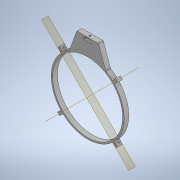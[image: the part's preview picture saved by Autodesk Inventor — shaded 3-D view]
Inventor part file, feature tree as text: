
AUTODESK INVENTOR PART (.ipt)
format: ipt  version: 2021.1 (Build 251245010, 245A)  size: 246,272 bytes
history: native  units: in
note: dims shown in document units (in); Inventor stores cm internally (conversion verified against a paired STEP export)
features: sketch x11, extrude x8, hole x2, plane x2, fillet x2, pattern_circular x1
ambient origin geometry x8: Origin, YZ Plane, XZ Plane, XY Plane, X Axis, Y Axis, Z Axis, Center Point
bodies: Solid1 (feature_tree)
feature tree (26):
  extrude  "Extrusion1"  Depth=0.75in TaperAngle=0.0deg
  extrude  "Extrusion2"  TaperAngle=0.0deg  [1 undecoded]
  extrude  "Extrusion3"  TaperAngle=45.0deg  [1 undecoded]
  extrude  "Extrusion4"  TaperAngle=45.0deg  [1 undecoded]
  sketch  "Sketch6"  dims[d47=0.25in d48=45.0deg]
  hole  "Hole2"  [1 undecoded]
  plane  "Work Plane1"
  plane  "Work Plane2"
  extrude  "Extrusion7"  Depth=0.25in TaperAngle=360.0deg
  hole  "Hole4"  [1 undecoded]
  pattern_circular  "Circular Pattern1"  Angle=30.0deg  [1 undecoded]
  extrude  "Extrusion8"  TaperAngle=30.0deg  [1 undecoded]
  sketch  "Sketch14"  dims[d65=0.0in d66=0.0in]
  extrude  "Extrusion9"  Depth=0.75in
  extrude  "Extrusion10"  TaperAngle=0.0deg  [1 undecoded]
  fillet  "Fillet1"  Radius=0.125in
  fillet  "Fillet2"  Radius=0.125in
  sketch  "Sketch1"  dims[d3=0.0in d7=0.75in d8=0.0in]
  sketch  "Sketch2"  dims[d9=2.5in d10=0.0in d22=0.0in]
  sketch  "Sketch5"  dims[d31=0.266in d32=0.75in d33=0.507in d34=0.25in d35=0.5635in d36=1.0in d37=0.8108in d45=45.0deg d46=-0.3092in]
  sketch  "Sketch7"  dims[d49=1.0in d50=135.0deg]
  sketch  "Sketch11"  dims[d51=0.75in d52=0.0in]
  sketch  "Sketch12"  dims[d53=0.201in d54=0.75in d55=0.507in d56=0.25in d57=0.5635in d58=1.0in d59=0.8108in d60=1.5748in d61=360.0deg]
  sketch  "Sketch13"  dims[d63=0.35in d64=0.1in]
  sketch  "Sketch15"  dims[d67=0.75in]
  sketch  "Sketch16"  dims[d68=0.0in d69=30.0deg d70=30.0deg d71=0.75in d72=0.0in d73=0.125in d74=0.125in]
note: 8 required parameter values undecoded (feature->parameter linkage not recoverable at this tier; creation-order binding heuristic only, values carry confidence <= 0.55)
